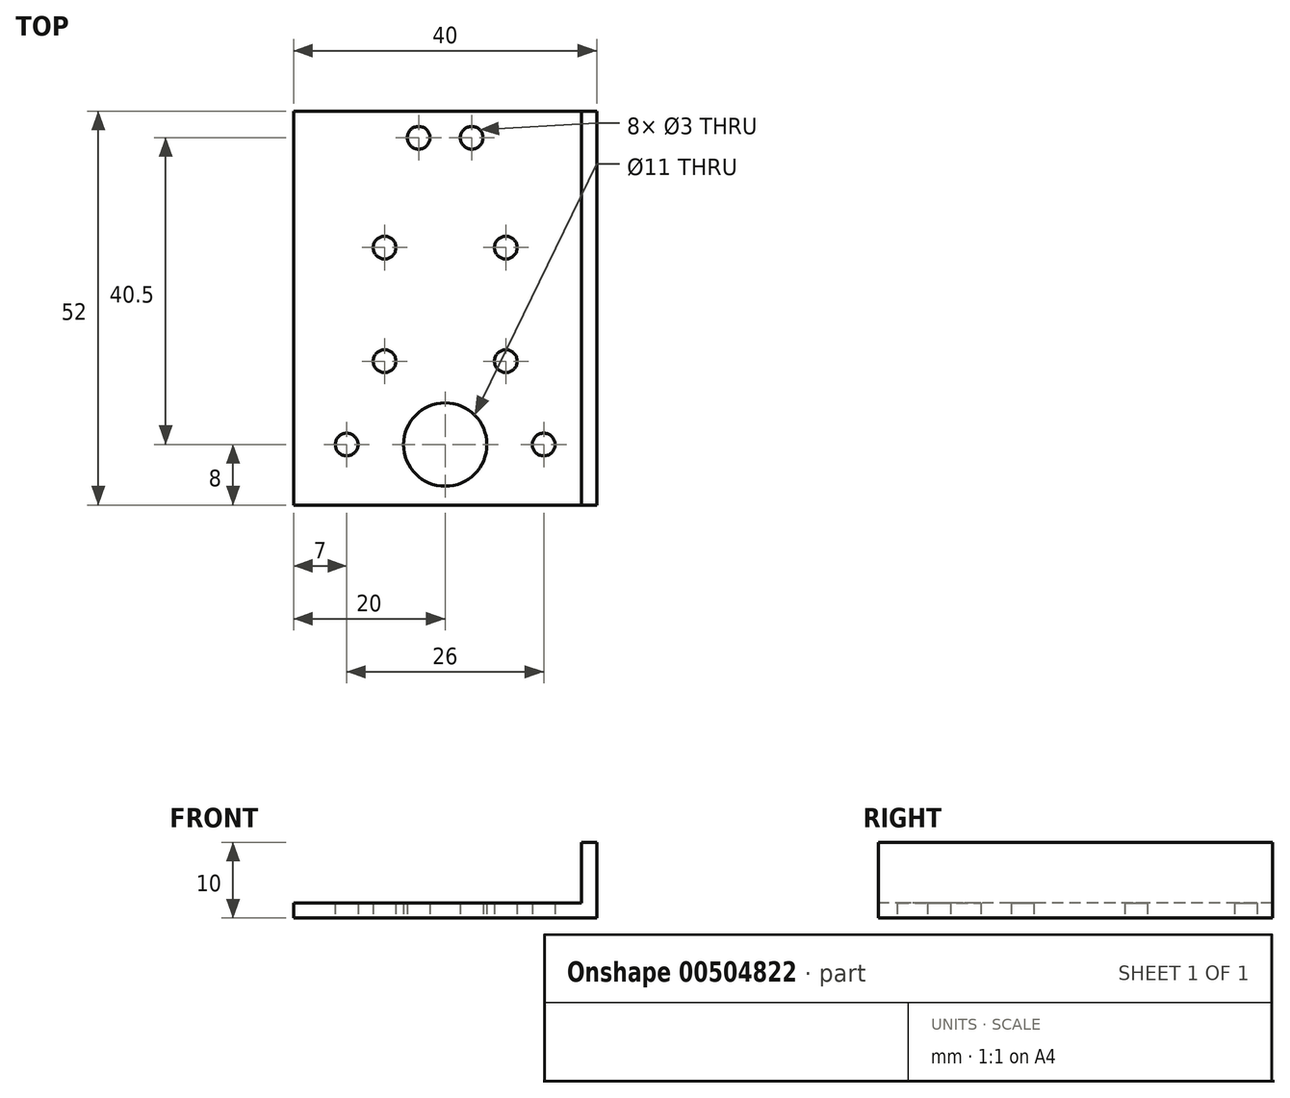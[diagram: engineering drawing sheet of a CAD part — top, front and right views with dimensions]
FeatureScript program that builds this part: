
annotation { "Feature Type Name" : "Feature", "Feature Type Description" : "" }
export const myFeature = defineFeature(function(context is Context, id is Id, definition is map)
    precondition{}
    {
        {
            var Q0;
            Q0=qCreatedBy(makeId("Top.planeOp"),FACE);
            var sketch = newSketch(context, id + "F0", { "sketchPlane" : qUnion([Q0])});
            skLineSegment(sketch, "E0.bottom", {"start": v(-20, 44) * mm, "end": v(20, 44) * mm});
            skLineSegment(sketch, "E0.top", {"start": v(-20, -8) * mm, "end": v(20, -8) * mm});
            skLineSegment(sketch, "E0.left", {"start": v(-20, 44) * mm, "end": v(-20, -8) * mm});
            skLineSegment(sketch, "E0.right", {"start": v(20, 44) * mm, "end": v(20, -8) * mm});
            skPoint(sketch, "E1", {"position": v(0, 44) * mm});
            skCircle(sketch, "E2", {"center": v(0, 0) * mm, "radius": 5.5 * mm});
            skCircle(sketch, "E3", {"center": v(-13, 0) * mm, "radius": 1.5 * mm});
            skCircle(sketch, "E4", {"center": v(13, 0) * mm, "radius": 1.5 * mm});
            skCircle(sketch, "E5", {"center": v(-8, 11) * mm, "radius": 1.5 * mm});
            skCircle(sketch, "E6", {"center": v(8, 11) * mm, "radius": 1.5 * mm});
            skCircle(sketch, "E7", {"center": v(-8, 26) * mm, "radius": 1.5 * mm});
            skCircle(sketch, "E8", {"center": v(8, 26) * mm, "radius": 1.5 * mm});
            skCircle(sketch, "E9", {"center": v(-3.5, 40.5) * mm, "radius": 1.5 * mm});
            skCircle(sketch, "E10", {"center": v(3.5, 40.5) * mm, "radius": 1.5 * mm});
            skSolve(sketch);
        }
        {
            var Q0;
            Q0=makeQuery(id+"F0.imprint","IMPRINT",FACE,{"disambiguationData":[TD([[makeQuery(id+"F0.imprint","IMPRINT",EDGE,{"derivedFrom":sQuery(id+"F0.wireOp",EDGE,"E0.bottom")}),-1.0]])]});
            extrude(context, id + "F1", {"entities" : qUnion([Q0]), "depth" : 2 * mm});
        }
        {
            var Q0;
            Q0=makeQuery(id+"F1.opExtrude","CAP_FACE",FACE,{"disambiguationData":[OSD([sQuery(id+"F0.wireOp",EDGE,"E0.bottom"),sQuery(id+"F0.wireOp",EDGE,"E0.top"),sQuery(id+"F0.wireOp",EDGE,"E0.left"),sQuery(id+"F0.wireOp",EDGE,"E0.right"),sQuery(id+"F0.wireOp",EDGE,"E2"),sQuery(id+"F0.wireOp",EDGE,"E3"),sQuery(id+"F0.wireOp",EDGE,"E4"),sQuery(id+"F0.wireOp",EDGE,"E5"),sQuery(id+"F0.wireOp",EDGE,"E6"),sQuery(id+"F0.wireOp",EDGE,"E7"),sQuery(id+"F0.wireOp",EDGE,"E8"),sQuery(id+"F0.wireOp",EDGE,"E9"),sQuery(id+"F0.wireOp",EDGE,"E10")])],"isStart":false});
            var sketch = newSketch(context, id + "F2", { "sketchPlane" : qUnion([Q0])});
            skLineSegment(sketch, "E11.bottom", {"start": v(18, 44) * mm, "end": v(20, 44) * mm});
            skLineSegment(sketch, "E11.top", {"start": v(18, -8) * mm, "end": v(20, -8) * mm});
            skLineSegment(sketch, "E11.left", {"start": v(18, 44) * mm, "end": v(18, -8) * mm});
            skLineSegment(sketch, "E11.right", {"start": v(20, 44) * mm, "end": v(20, -8) * mm});
            skSolve(sketch);
        }
        {
            var Q0;
            Q0=makeQuery(id+"F2.imprint","IMPRINT",FACE,{"disambiguationData":[TD([[makeQuery(id+"F2.imprint","IMPRINT",EDGE,{"derivedFrom":sQuery(id+"F2.wireOp",EDGE,"E11.bottom")}),-1.0]])]});
            extrude(context, id + "F3", {"entities" : qUnion([Q0]), "operationType" : NewBodyOperationType.ADD, "depth" : 8 * mm});
        }
    });
